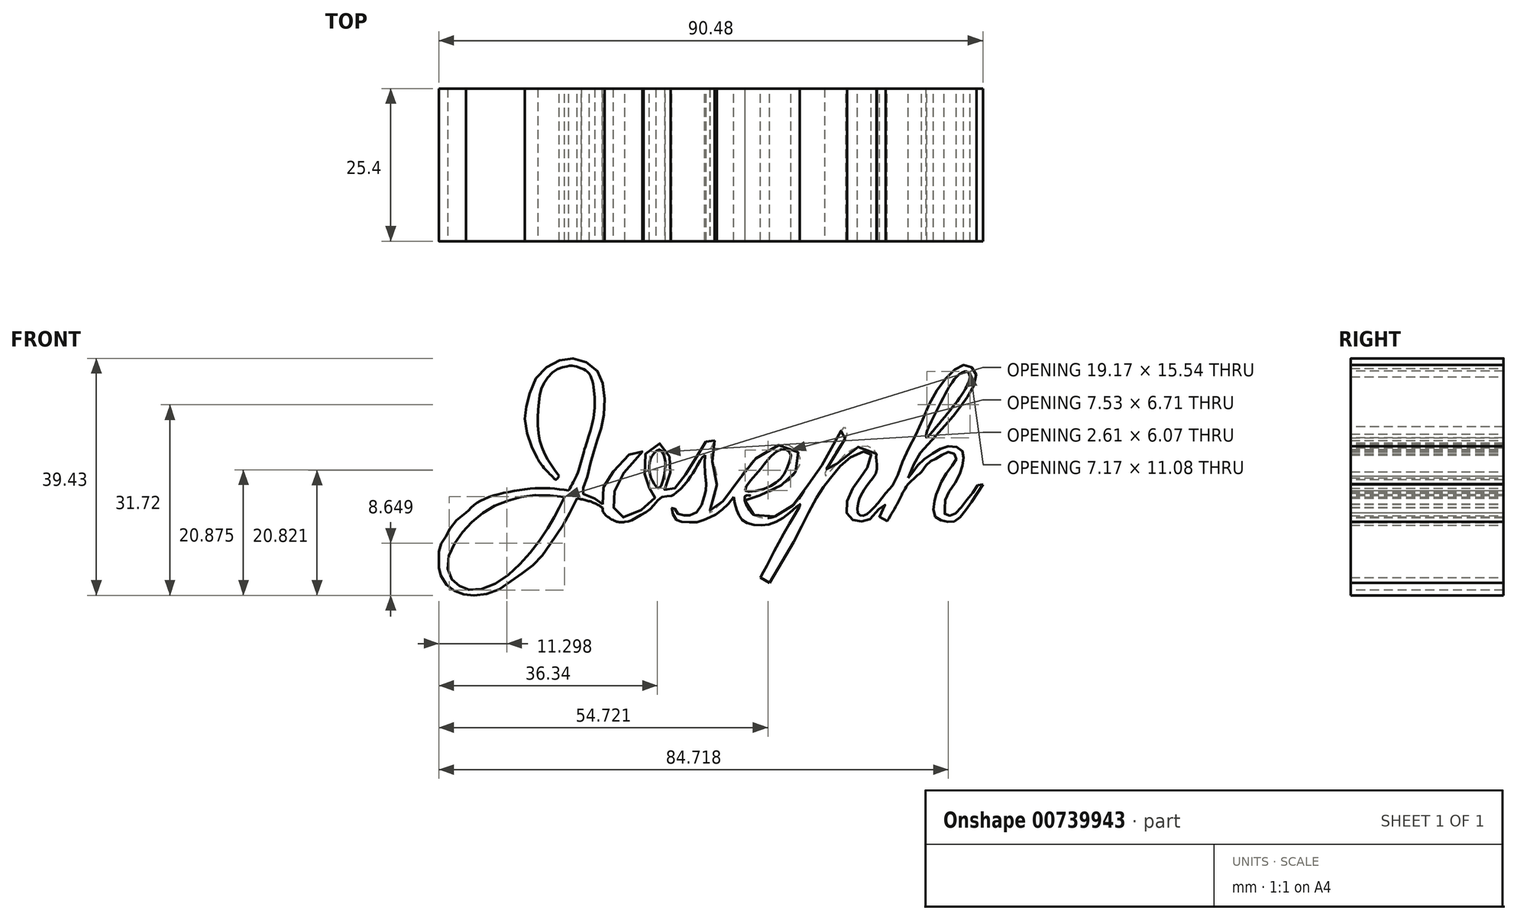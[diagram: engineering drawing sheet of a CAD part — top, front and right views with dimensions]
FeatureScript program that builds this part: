
annotation { "Feature Type Name" : "Feature", "Feature Type Description" : "" }
export const myFeature = defineFeature(function(context is Context, id is Id, definition is map)
    precondition{}
    {
        {
            var Q0;
            Q0=qCreatedBy(makeId("Front.planeOp"),FACE);
            var sketch = newSketch(context, id + "F0", { "sketchPlane" : qUnion([Q0])});
            skFitSpline(sketch, "E0", {"points": [v(-24.19, 2.62) * mm, v(-28.53, 2.99) * mm, v(-32.66, 2.32) * mm, v(-36.27, 0.92) * mm, v(-39.58, -1.5) * mm, v(-42.01, -4.45) * mm, v(-43.56, -7.84) * mm, v(-43.12, -10.79) * mm, v(-41.57, -12.19) * mm, v(-39.36, -12.85) * mm, v(-35.46, -11.67) * mm, v(-31.55, -8.5) * mm, v(-28.53, -4.9) * mm, v(-26.25, -1.36) * mm, v(-25.07, 0.85) * mm], "startDerivative": vector(-55.85, 7.8) * mm, "endDerivative": vector(17.96, 35.26) * mm});
            skFitSpline(sketch, "E1", {"points": [v(-24.19, 2.62) * mm, v(-25.07, 0.85) * mm], "startDerivative": vector(-0.88, -1.77) * mm, "endDerivative": vector(-0.88, -1.77) * mm});
            skFitSpline(sketch, "E2", {"points": [v(-23.5, 3.73) * mm, v(-28.09, 4.1) * mm, v(-33.73, 3.42) * mm, v(-38.37, 1.88) * mm, v(-40.54, 0) * mm], "startDerivative": vector(-17.51, 2.27) * mm, "endDerivative": vector(-9.35, -10) * mm});
            skFitSpline(sketch, "E3", {"points": [v(-40.54, 0) * mm, v(-42.96, -2.15) * mm, v(-43.89, -3.95) * mm, v(-44.75, -5.31) * mm, v(-45.06, -6.86) * mm, v(-45.06, -8.53) * mm, v(-45, -9.7) * mm, v(-43.89, -11.83) * mm, v(-41.94, -13.23) * mm, v(-39.7, -13.72) * mm, v(-36.02, -13.18) * mm, v(-32.27, -10.79) * mm, v(-28.8, -8.17) * mm, v(-26.3, -4.75) * mm, v(-24.57, -2.28) * mm, v(-22.1, 2.42) * mm], "startDerivative": vector(-38.92, -28.89) * mm, "endDerivative": vector(27.39, 56.27) * mm});
            skFitSpline(sketch, "E4", {"points": [v(-22.1, 2.42) * mm, v(-19.44, 1.72) * mm, v(-17.86, 0.85) * mm], "startDerivative": vector(5.2, -1.08) * mm, "endDerivative": vector(3.24, -2.1) * mm});
            skFitSpline(sketch, "E5", {"points": [v(-17.86, 0.85) * mm, v(-17.66, 0) * mm, v(-16.46, -1.01) * mm, v(-15.19, -1.54) * mm, v(-14.11, -1.52) * mm], "startDerivative": vector(0.2, -4.04) * mm, "endDerivative": vector(4.53, 0.52) * mm});
            skFitSpline(sketch, "E6", {"points": [v(-23.5, 3.73) * mm, v(-22.1, 6.35) * mm, v(-21.07, 9.81) * mm, v(-20.04, 13.13) * mm], "startDerivative": vector(4.83, 7.9) * mm, "endDerivative": vector(3.15, 9.58) * mm});
            skFitSpline(sketch, "E7", {"points": [v(-20.04, 13.13) * mm, v(-19.26, 16.53) * mm, v(-19.26, 20.29) * mm, v(-20.04, 23.09) * mm, v(-21.36, 24.04) * mm], "startDerivative": vector(3.41, 12.14) * mm, "endDerivative": vector(-7.81, 3.81) * mm});
            skFitSpline(sketch, "E8", {"points": [v(-21.36, 24.04) * mm, v(-23.09, 24.52) * mm, v(-23.5, 24.4) * mm, v(-25.07, 24.04) * mm, v(-27.54, 21.68) * mm, v(-28.47, 18.15) * mm, v(-28.5, 13.13) * mm, v(-27.14, 9.17) * mm, v(-25.07, 6.1) * mm], "startDerivative": vector(-20.51, 7.15) * mm, "endDerivative": vector(15.1, -20.32) * mm});
            skFitSpline(sketch, "E9", {"points": [v(-25.07, 6.1) * mm, v(-25.64, 5.5) * mm, v(-25.9, 5.73) * mm, v(-26.25, 6.1) * mm, v(-27.53, 7.39) * mm, v(-28.46, 8.68) * mm, v(-28.74, 9.17) * mm], "startDerivative": vector(-3.8, -5.4) * mm, "endDerivative": vector(-1.72, 3.29) * mm});
            skFitSpline(sketch, "E10", {"points": [v(-28.74, 9.17) * mm, v(-29.97, 11.86) * mm, v(-30.78, 15.7) * mm, v(-30.34, 18.53) * mm, v(-28.74, 22.67) * mm, v(-25.42, 25.2) * mm, v(-22.1, 25.6) * mm, v(-18.9, 23.8) * mm, v(-17.66, 20.65) * mm, v(-17.66, 15.9) * mm, v(-18.47, 12.9) * mm, v(-19.26, 10.42) * mm, v(-20.04, 7.62) * mm, v(-20.87, 4.51) * mm, v(-21.36, 3.37) * mm, v(-19.26, 2.42) * mm, v(-17.86, 1.44) * mm], "startDerivative": vector(-21.02, 40.61) * mm, "endDerivative": vector(24.08, -22.55) * mm});
            skFitSpline(sketch, "E11", {"points": [v(-17.86, 1.44) * mm, v(-17.86, 3.73) * mm, v(-16.6, 6.1) * mm, v(-14.68, 8.54) * mm, v(-11.52, 10.73) * mm, v(-11.3, 9.81) * mm, v(-11.96, 9.17) * mm, v(-13.01, 8.1) * mm, v(-14.94, 5.78) * mm, v(-16.04, 2.82) * mm, v(-16, 0.85) * mm, v(-15.38, -0.48) * mm, v(-12.7, -0.4) * mm, v(-10.42, 1.44) * mm, v(-9.01, 2.82) * mm, v(-9.71, 3.73) * mm, v(-10.46, 5.03) * mm, v(-10.94, 6.91) * mm, v(-10.49, 10.29) * mm, v(-8.43, 11.56) * mm, v(-6.85, 9.81) * mm, v(-6.59, 8.4) * mm, v(-6.8, 5.6) * mm, v(-7.55, 3.73) * mm, v(-6.72, 3.73) * mm, v(-5.32, 4.5) * mm, v(-3.83, 6.83) * mm, v(-1.9, 9.81) * mm, v(-0.72, 11.73) * mm, v(0, 12.48) * mm, v(0.77, 12.04) * mm], "startDerivative": vector(-8.25, 65.4) * mm, "endDerivative": vector(36.42, -32) * mm});
            skFitSpline(sketch, "E12", {"points": [v(-8.47, 4.11) * mm, v(-7.5, 6.78) * mm, v(-7.55, 9.17) * mm, v(-8.3, 10.5) * mm, v(-9.35, 9.81) * mm, v(-9.96, 8.53) * mm, v(-10, 6.65) * mm, v(-9.44, 5.07) * mm, v(-8.47, 4.11) * mm]});
            skFitSpline(sketch, "E13", {"points": [v(-14.11, -1.52) * mm, v(-13.28, -1.36) * mm, v(-11.54, -0.4) * mm, v(-9.71, 0.85) * mm, v(-8.01, 2.62) * mm, v(-6.3, 2.82) * mm, v(-5.86, 3.11) * mm, v(-4.39, 4.51) * mm, v(-3.2, 6.1) * mm, v(-2.49, 7.2) * mm, v(-1.51, 8.87) * mm, v(-0.83, 9.6) * mm], "startDerivative": vector(11.57, 0.88) * mm, "endDerivative": vector(9.2, 8.33) * mm});
            skFitSpline(sketch, "E14", {"points": [v(-0.83, 9.6) * mm, v(-0.83, 7.08) * mm, v(-0.63, 4.11) * mm, v(-0.83, 3.22) * mm, v(-1.58, 0.85) * mm, v(-3.2, -0.4) * mm, v(-4.39, -0.4) * mm, v(-5.48, 0) * mm, v(-5.96, 0.85) * mm, v(-6.31, 0.85) * mm, v(-6.05, -0.4) * mm, v(-5.35, -1.36) * mm, v(-3.83, -1.54) * mm, v(-1.9, -1.54) * mm, v(-0.44, -0.93) * mm, v(0.77, -0.4) * mm, v(2.45, 0.85) * mm, v(3.94, 2.62) * mm], "startDerivative": vector(-1.28, -31.31) * mm, "endDerivative": vector(19.57, 25.65) * mm});
            skFitSpline(sketch, "E15", {"points": [v(0.77, 12.04) * mm, v(0, 9.81) * mm, v(0.77, 7.72) * mm, v(1.16, 5.1) * mm, v(0.77, 2.62) * mm, v(0, 0) * mm, v(1.15, 0.85) * mm, v(3.25, 3.27) * mm, v(5.2, 6.1) * mm, v(7.08, 8.54) * mm, v(9.93, 10.6) * mm, v(12.3, 11.4) * mm, v(14.3, 10.6) * mm, v(14.97, 8.67) * mm, v(14.48, 7.2) * mm, v(12.78, 5.17) * mm, v(12.03, 4.73) * mm, v(10.52, 3.73) * mm, v(7.45, 2.82) * mm, v(5.89, 2.82) * mm, v(5.89, 1.79) * mm, v(6.3, 0.85) * mm, v(7.45, -0.4) * mm, v(9.74, -0.83) * mm, v(11.2, -0.4) * mm, v(13.18, 0.85) * mm, v(14.43, 1.79) * mm, v(16.36, 4.74) * mm, v(17.35, 6.1) * mm, v(20.12, 10.46) * mm, v(22.47, 14.3) * mm, v(22.78, 13.13) * mm, v(21.24, 10.7) * mm, v(19.07, 6.1) * mm, v(21.42, 8.6) * mm, v(23.84, 10.64) * mm, v(26.56, 11.08) * mm, v(27.68, 9.81) * mm], "startDerivative": vector(-45.14, -84.77) * mm, "endDerivative": vector(37.07, -70.29) * mm});
            skFitSpline(sketch, "E16", {"points": [v(5.89, 3.73) * mm, v(8.04, 6.83) * mm, v(9.93, 9.17) * mm, v(12.19, 10.6) * mm, v(13.43, 9.81) * mm, v(13.24, 8.54) * mm, v(12.06, 6.1) * mm, v(9.27, 4.11) * mm, v(5.89, 3.73) * mm]});
            skFitSpline(sketch, "E17", {"points": [v(3.94, 2.62) * mm, v(4.63, 0) * mm, v(5.89, -1.54) * mm, v(9.21, -2.03) * mm, v(12.78, -0.4) * mm, v(15.04, 1.44) * mm, v(12.78, -2.58) * mm, v(9.93, -7.91) * mm, v(8.39, -10.79) * mm], "startDerivative": vector(5.24, -25.36) * mm, "endDerivative": vector(-12.3, -22.45) * mm});
            skFitSpline(sketch, "E18", {"points": [v(8.39, -10.79) * mm, v(9.93, -11.67) * mm], "startDerivative": vector(1.54, -0.88) * mm, "endDerivative": vector(1.54, -0.88) * mm});
            skFitSpline(sketch, "E19", {"points": [v(9.93, -11.67) * mm, v(14.43, -3.85) * mm, v(16.36, 0) * mm, v(18.5, 3.73) * mm, v(19.57, 5.17) * mm, v(21.96, 8.05) * mm, v(24.5, 9.81) * mm, v(26.7, 10.06) * mm, v(26.26, 7.7) * mm, v(24.84, 5.63) * mm, v(23.14, 2.82) * mm, v(22.7, 0.16) * mm, v(23.58, -1.06) * mm, v(24.83, -1.36) * mm, v(26.08, -1.36) * mm, v(27.68, 0.16) * mm, v(29.14, 1.44) * mm, v(28.18, -0.77) * mm, v(29.47, -1.36) * mm], "startDerivative": vector(49.75, 83.82) * mm, "endDerivative": vector(46.79, -3.81) * mm});
            skFitSpline(sketch, "E20", {"points": [v(29.47, -1.36) * mm, v(31.31, 1.79) * mm, v(32.75, 4.45) * mm, v(35.22, 6.83) * mm], "startDerivative": vector(5.7, 9.16) * mm, "endDerivative": vector(8.15, 6.73) * mm});
            skFitSpline(sketch, "E21", {"points": [v(35.22, 6.83) * mm, v(36.58, 8.54) * mm, v(37.88, 9.17) * mm, v(39.9, 10.13) * mm, v(40.97, 9.17) * mm, v(39.46, 6.83) * mm, v(37.92, 3.73) * mm, v(37.44, 2.42) * mm, v(37.35, -0.4) * mm, v(38.92, -1.36) * mm, v(40.76, -1.36) * mm, v(42.87, 0.85) * mm, v(45.4, 4.74) * mm], "startDerivative": vector(16.44, 25.36) * mm, "endDerivative": vector(21.75, 34.23) * mm});
            skFitSpline(sketch, "E22", {"points": [v(45.4, 4.74) * mm, v(44.75, 4.74) * mm, v(43.7, 3.3) * mm, v(42.47, 1.79) * mm, v(41.16, 0.16) * mm, v(40.33, -0.4) * mm, v(39.36, -0.4) * mm, v(38.97, 0) * mm, v(39.05, 0.85) * mm, v(39.27, 2.62) * mm, v(40.63, 4.74) * mm, v(41.68, 6.83) * mm, v(42.12, 8.54) * mm, v(42.12, 9.81) * mm, v(41.64, 10.7) * mm, v(39.98, 11.1) * mm, v(38.43, 10.7) * mm, v(36.63, 9.6) * mm, v(34.86, 8.23) * mm, v(33.8, 6.83) * mm, v(32.94, 5.84) * mm], "startDerivative": vector(-20.1, 5.48) * mm, "endDerivative": vector(-18.4, -19.95) * mm});
            skFitSpline(sketch, "E23", {"points": [v(32.94, 5.84) * mm, v(34.89, 9.81) * mm, v(36.73, 11.89) * mm, v(39.16, 14.61) * mm, v(41.37, 17.26) * mm, v(43.14, 19.84) * mm, v(44.32, 22.86) * mm, v(43.43, 24.26) * mm, v(41.96, 24.56) * mm, v(39.75, 22.94) * mm, v(36.95, 19.03) * mm, v(34.52, 13.5) * mm, v(32.16, 8.87) * mm, v(30.76, 5.18) * mm, v(29.21, 3.27) * mm], "startDerivative": vector(22.72, 53.9) * mm, "endDerivative": vector(-27.66, -27.71) * mm});
            skFitSpline(sketch, "E24", {"points": [v(29.21, 3.27) * mm, v(26.93, 0.52) * mm, v(25.42, -0.47) * mm, v(24.59, 0) * mm, v(24.85, 2.24) * mm, v(25.32, 3.27) * mm, v(26.04, 4.45) * mm, v(27.68, 6.83) * mm, v(27.68, 8.65) * mm, v(27.68, 9.81) * mm], "startDerivative": vector(-14.84, -19.16) * mm, "endDerivative": vector(0.74, 12.36) * mm});
            skFitSpline(sketch, "E25", {"points": [v(36.1, 12.45) * mm, v(42.5, 20.63) * mm, v(43.23, 22.6) * mm], "startDerivative": vector(11.69, 13.76) * mm, "endDerivative": vector(1.27, 5.52) * mm});
            skFitSpline(sketch, "E26", {"points": [v(43.23, 22.6) * mm, v(42.85, 23.5) * mm, v(41.68, 23.2) * mm, v(40.07, 21.42) * mm, v(38.67, 18.86) * mm, v(35.92, 12.84) * mm, v(36.1, 12.45) * mm], "startDerivative": vector(-1.9, 9.9) * mm, "endDerivative": vector(3.82, -3.1) * mm});
            skSolve(sketch);
        }
        {
            var Q0;
            Q0 = qSketchRegion(id + "F0", true);
            extrude(context, id + "F1", {"entities" : qUnion([Q0]), "depth" : 25.4 * mm, "offsetDistance" : 25.4 * mm});
        }
    });
